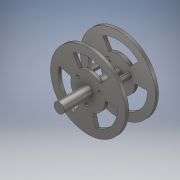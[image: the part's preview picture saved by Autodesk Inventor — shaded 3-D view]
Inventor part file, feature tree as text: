
AUTODESK INVENTOR PART (.ipt)
format: ipt  version: 2019 (Build 230136000, 136)  size: 245,760 bytes
history: native  units: mm
features: extrude x5, sketch x4, projected_geometry x2
ambient origin geometry x8: Origin, YZ Plane, XZ Plane, XY Plane, X Axis, Y Axis, Z Axis, Center Point
bodies: Solid1 (feature_tree)
feature tree (11):
  sketch  "Sketch1"  dims[d0=48.0mm d1=7.0mm]
  extrude  "Extrusion1"  Depth=7.0mm
  extrude  "Extrusion2"  Depth=19.0mm
  extrude  "Extrusion3"  Depth=30.0mm TaperAngle=360.0deg
  extrude  "Extrusion4"  Depth=18.5mm
  extrude  "Extrusion5"  TaperAngle=22.5deg  [1 undecoded]
  sketch  "Sketch2"  dims[d2=11.0mm d4=19.0mm]
  projected_geometry  "Projected Loop1"
  sketch  "Sketch3"  dims[d5=75.0deg d6=30.0mm d8=360.0deg]
  projected_geometry  "Projected Loop2"
  sketch  "Sketch4"  dims[d10=2.0mm d11=8.0mm d12=22.5deg d13=30.0mm d15=360.0deg d17=2.0mm d18=0.0mm d19=21.0mm d20=0.0mm d21=2.0mm d22=0.0mm d23=3.0mm d24=30.0mm d26=360.0deg d28=17.0mm d29=0.0mm d30=6.5mm d31=18.5mm d32=0.0mm]
note: 1 required parameter value undecoded (feature->parameter linkage not recoverable at this tier; creation-order binding heuristic only, values carry confidence <= 0.55)
